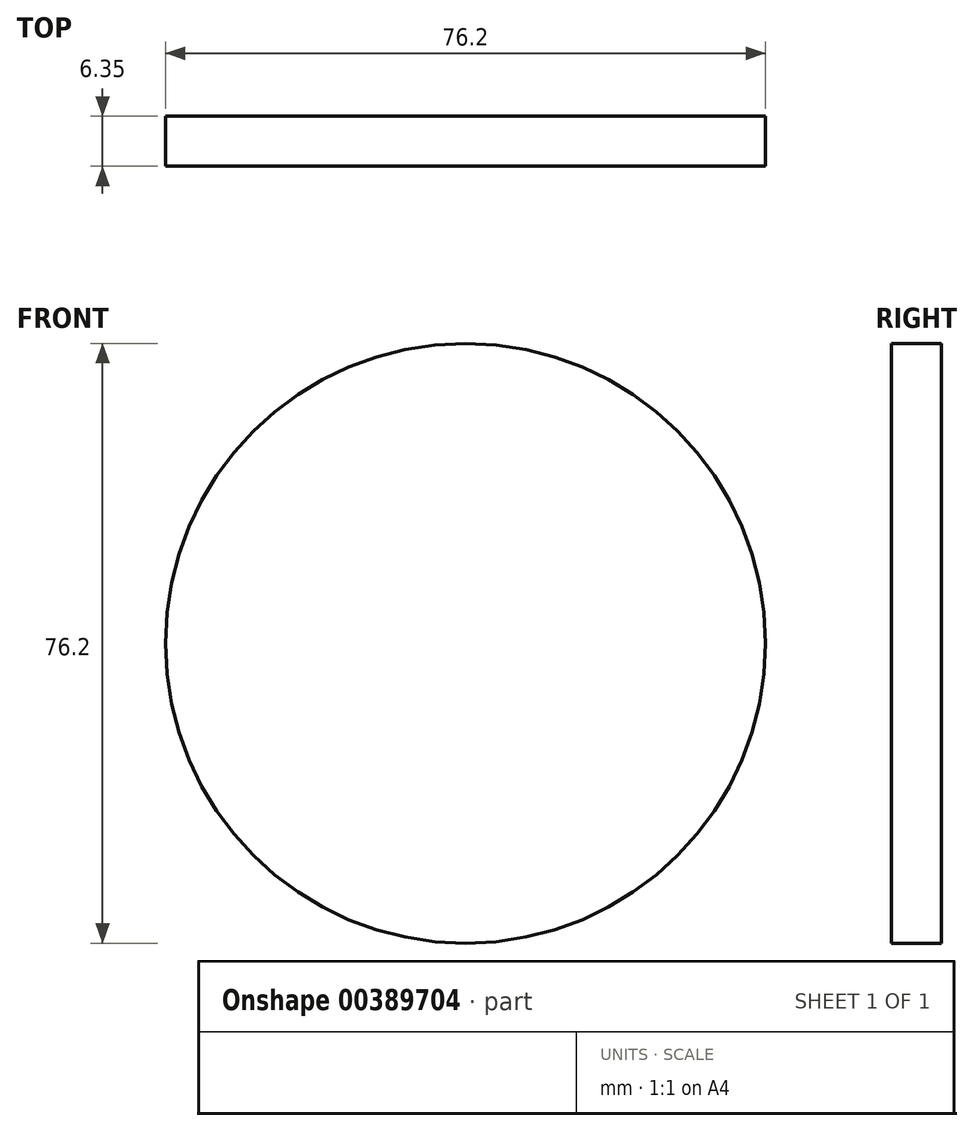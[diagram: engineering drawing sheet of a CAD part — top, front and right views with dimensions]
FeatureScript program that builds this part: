
annotation { "Feature Type Name" : "Feature", "Feature Type Description" : "" }
export const myFeature = defineFeature(function(context is Context, id is Id, definition is map)
    precondition{}
    {
        {
            var Q0;
            Q0=qCreatedBy(makeId("Front.planeOp"),FACE);
            var sketch = newSketch(context, id + "F0", { "sketchPlane" : qUnion([Q0])});
            skCircle(sketch, "E0", {"center": v(0, 0) * mm, "radius": 38.1 * mm});
            skSolve(sketch);
        }
        {
            var Q0;
            Q0=sQuery(id+"F0.wireOp",EDGE,"E0");
            extrude(context, id + "F1", {"bodyType" : ToolBodyType.SURFACE, "surfaceEntities" : qUnion([Q0]), "depth" : 57.15 * mm, "offsetDistance" : 25.4 * mm});
        }
        {
            var Q0;
            Q0=qCreatedBy(makeId("Front.planeOp"),FACE);
            var sketch = newSketch(context, id + "F2", { "sketchPlane" : qUnion([Q0])});
            skCircle(sketch, "E1", {"center": v(0, 0) * mm, "radius": 38.1 * mm});
            skSolve(sketch);
        }
        {
            var Q0;
            Q0 = qSketchRegion(id + "F2", true);
            extrude(context, id + "F3", {"entities" : qUnion([Q0]), "depth" : 6.35 * mm, "offsetDistance" : 25.4 * mm});
        }
    });
